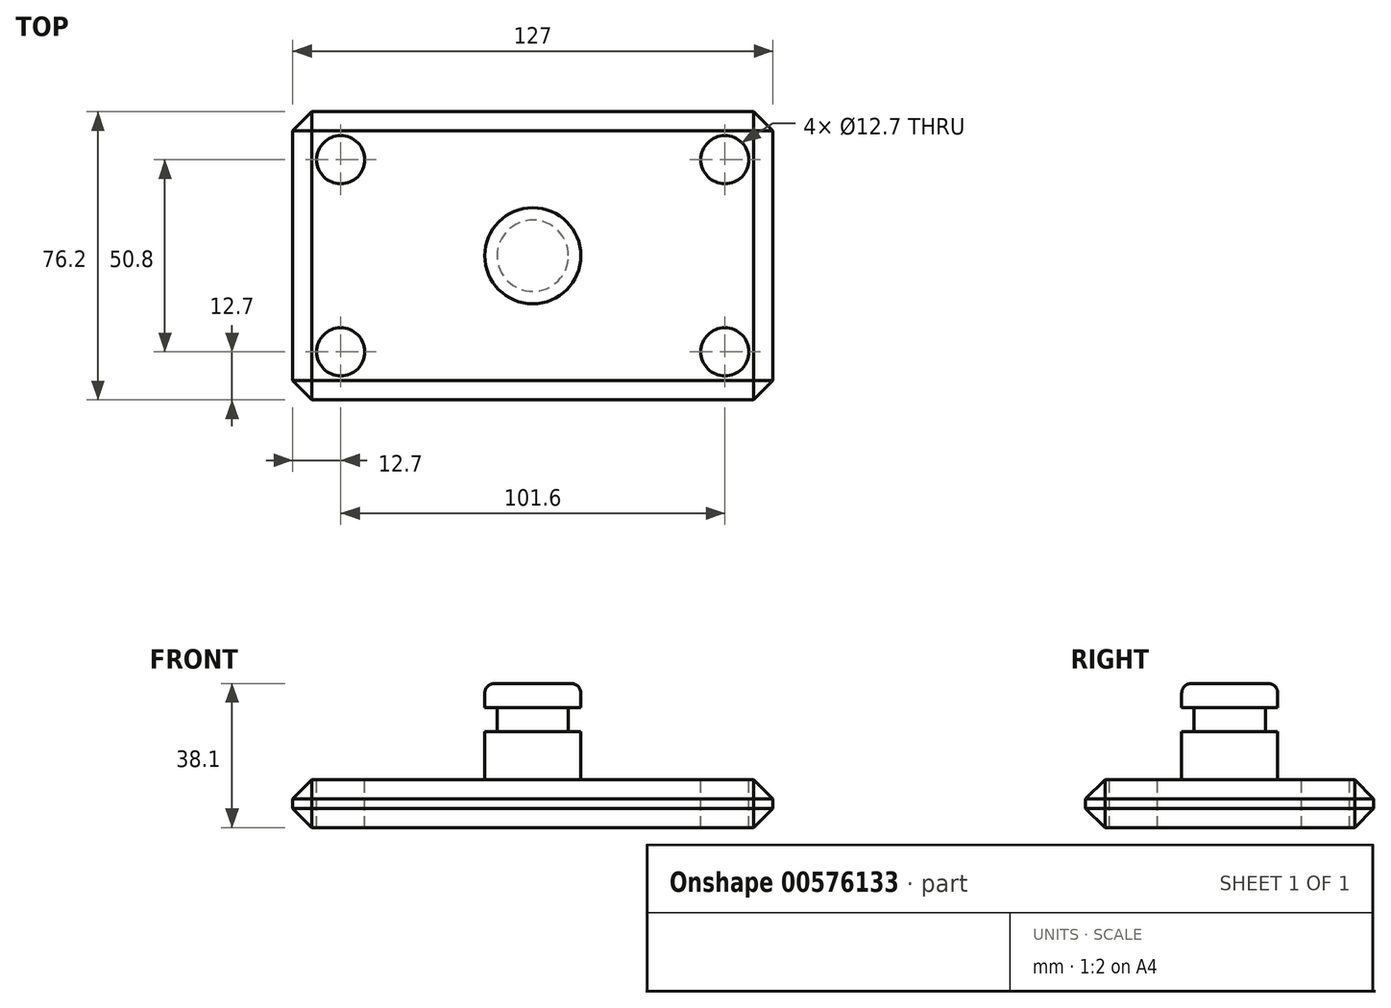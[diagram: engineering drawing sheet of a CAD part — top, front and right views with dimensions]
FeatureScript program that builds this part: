
annotation { "Feature Type Name" : "Feature", "Feature Type Description" : "" }
export const myFeature = defineFeature(function(context is Context, id is Id, definition is map)
    precondition{}
    {
        {
            var Q0;
            Q0=qCreatedBy(makeId("Top.planeOp"),FACE);
            var sketch = newSketch(context, id + "F0", { "sketchPlane" : qUnion([Q0])});
            skLineSegment(sketch, "E0.bottom", {"start": v(-63.5, 38.1) * mm, "end": v(63.5, 38.1) * mm});
            skLineSegment(sketch, "E0.top", {"start": v(-63.5, -38.1) * mm, "end": v(63.5, -38.1) * mm});
            skLineSegment(sketch, "E0.left", {"start": v(-63.5, -38.1) * mm, "end": v(-63.5, 38.1) * mm});
            skLineSegment(sketch, "E0.right", {"start": v(63.5, -38.1) * mm, "end": v(63.5, 38.1) * mm});
            skPoint(sketch, "E0.middle", {"position": v(0, 0) * mm});
            skSolve(sketch);
        }
        {
            var Q0;
            Q0=makeQuery(id+"F0.imprint","IMPRINT",FACE,{"disambiguationData":[TD([[makeQuery(id+"F0.imprint","IMPRINT",EDGE,{"derivedFrom":sQuery(id+"F0.wireOp",EDGE,"E0.bottom")}),-1.0]])]});
            extrude(context, id + "F1", {"entities" : qUnion([Q0]), "depth" : 12.7 * mm, "offsetDistance" : 25.4 * mm});
        }
        {
            var Q0;
            Q0=makeQuery(id+"F1.opExtrude","CAP_FACE",FACE,{"disambiguationData":[OSD([sQuery(id+"F0.wireOp",EDGE,"E0.bottom"),sQuery(id+"F0.wireOp",EDGE,"E0.top"),sQuery(id+"F0.wireOp",EDGE,"E0.left"),sQuery(id+"F0.wireOp",EDGE,"E0.right")])],"isStart":false});
            var sketch = newSketch(context, id + "F2", { "sketchPlane" : qUnion([Q0])});
            skCircle(sketch, "E1", {"center": v(-50.8, 25.4) * mm, "radius": 6.35 * mm});
            skCircle(sketch, "E2", {"center": v(50.8, 25.4) * mm, "radius": 6.35 * mm});
            skCircle(sketch, "E3", {"center": v(50.8, -25.4) * mm, "radius": 6.35 * mm});
            skCircle(sketch, "E4", {"center": v(-50.8, -25.4) * mm, "radius": 6.35 * mm});
            skSolve(sketch);
        }
        {
            var Q0;
            Q0=makeQuery(id+"F2.imprint","IMPRINT",FACE,{"disambiguationData":[TD([[makeQuery(id+"F2.imprint","IMPRINT",EDGE,{"derivedFrom":sQuery(id+"F2.wireOp",EDGE,"E1")}),1.0]])]});
            var Q1;
            Q1=makeQuery(id+"F2.imprint","IMPRINT",FACE,{"disambiguationData":[TD([[makeQuery(id+"F2.imprint","IMPRINT",EDGE,{"derivedFrom":sQuery(id+"F2.wireOp",EDGE,"E2")}),1.0]])]});
            var Q2;
            Q2=makeQuery(id+"F2.imprint","IMPRINT",FACE,{"disambiguationData":[TD([[makeQuery(id+"F2.imprint","IMPRINT",EDGE,{"derivedFrom":sQuery(id+"F2.wireOp",EDGE,"E3")}),1.0]])]});
            var Q3;
            Q3=makeQuery(id+"F2.imprint","IMPRINT",FACE,{"disambiguationData":[TD([[makeQuery(id+"F2.imprint","IMPRINT",EDGE,{"derivedFrom":sQuery(id+"F2.wireOp",EDGE,"E4")}),1.0]])]});
            extrude(context, id + "F3", {"entities" : qUnion([Q0, Q1, Q2, Q3]), "operationType" : NewBodyOperationType.REMOVE, "endBound" : BoundingType.THROUGH_ALL, "oppositeDirection" : true, "depth" : 25.4 * mm, "offsetDistance" : 25.4 * mm});
        }
        {
            var Q0;
            Q0=qCreatedBy(makeId("Front.planeOp"),FACE);
            var sketch = newSketch(context, id + "F4", { "sketchPlane" : qUnion([Q0])});
            skLineSegment(sketch, "E5.bottom", {"start": v(0, 12.7) * mm, "end": v(12.7, 12.7) * mm});
            skLineSegment(sketch, "E5.top", {"start": v(0, 38.1) * mm, "end": v(12.7, 38.1) * mm});
            skLineSegment(sketch, "E5.left", {"start": v(0, 12.7) * mm, "end": v(0, 38.1) * mm});
            skLineSegment(sketch, "E5.right", {"start": v(12.7, 12.7) * mm, "end": v(12.7, 38.1) * mm});
            skSolve(sketch);
        }
        {
            var Q0;
            Q0=makeQuery(id+"F4.imprint","IMPRINT",FACE,{"disambiguationData":[TD([[makeQuery(id+"F4.imprint","IMPRINT",EDGE,{"derivedFrom":sQuery(id+"F4.wireOp",EDGE,"E5.bottom")}),1.0]])]});
            var Q1;
            Q1=sQuery(id+"F4.wireOp",EDGE,"E5.left");
            revolve(context, id + "F5", {"operationType" : NewBodyOperationType.ADD, "entities" : qUnion([Q0]), "axis" : qUnion([Q1]), "revolveType" : RevolveType.FULL});
        }
        {
            var Q0;
            Q0=qCreatedBy(makeId("Front.planeOp"),FACE);
            var sketch = newSketch(context, id + "F6", { "sketchPlane" : qUnion([Q0])});
            skLineSegment(sketch, "E6.bottom", {"start": v(9.43, 31.75) * mm, "end": v(15.78, 31.75) * mm});
            skLineSegment(sketch, "E6.top", {"start": v(9.43, 25.4) * mm, "end": v(15.78, 25.4) * mm});
            skLineSegment(sketch, "E6.left", {"start": v(9.43, 31.75) * mm, "end": v(9.43, 25.4) * mm});
            skLineSegment(sketch, "E6.right", {"start": v(15.78, 31.75) * mm, "end": v(15.78, 25.4) * mm});
            skSolve(sketch);
        }
        {
            var Q0;
            Q0=makeQuery(id+"F6.imprint","IMPRINT",FACE,{"disambiguationData":[TD([[makeQuery(id+"F6.imprint","IMPRINT",EDGE,{"derivedFrom":sQuery(id+"F6.wireOp",EDGE,"E6.bottom")}),-1.0]])]});
            var Q1;
            Q1=makeQuery(id+"F5.opRevolve","SWEPT_FACE",FACE,{"disambiguationData":[OSD([sQuery(id+"F4.wireOp",EDGE,"E5.right")])]});
            revolve(context, id + "F7", {"operationType" : NewBodyOperationType.REMOVE, "entities" : qUnion([Q0]), "axis" : qUnion([Q1]), "revolveType" : RevolveType.FULL, "oppositeDirection" : true});
        }
        {
            var Q0;
            Q0=makeQuery(id+"F5.opRevolve","SWEPT_FACE",FACE,{"disambiguationData":[OSD([sQuery(id+"F4.wireOp",EDGE,"E5.top")])]});
            var Q1;
            Q1=makeQuery(id+"F5.opRevolve","SWEPT_EDGE",EDGE,{"disambiguationData":[OSD([sQuery(id+"F4.wireOp",EDGE,"E5.bottom"),sQuery(id+"F4.wireOp",EDGE,"E5.right")])]});
            var Q2;
            Q2=makeQuery(id+"F5.opRevolve","SWEPT_EDGE",EDGE,{"disambiguationData":[OSD([sQuery(id+"F4.wireOp",EDGE,"E5.top"),sQuery(id+"F4.wireOp",EDGE,"E5.right")])]});
            fillet(context, id + "F8", {"entities" : qUnion([Q0, Q1, Q2]), "radius" : 2.54 * mm, "tangentPropagation" : true, "allowEdgeOverflow" : false});
        }
        {
            var Q0;
            Q0=makeQuery(id+"F1.opExtrude","SWEPT_FACE",FACE,{"disambiguationData":[OSD([sQuery(id+"F0.wireOp",EDGE,"E0.bottom")])]});
            var Q1;
            Q1=makeQuery(id+"F1.opExtrude","SWEPT_FACE",FACE,{"disambiguationData":[OSD([sQuery(id+"F0.wireOp",EDGE,"E0.right")])]});
            var Q2;
            Q2=makeQuery(id+"F1.opExtrude","SWEPT_FACE",FACE,{"disambiguationData":[OSD([sQuery(id+"F0.wireOp",EDGE,"E0.left")])]});
            var Q3;
            Q3=makeQuery(id+"F1.opExtrude","SWEPT_FACE",FACE,{"disambiguationData":[OSD([sQuery(id+"F0.wireOp",EDGE,"E0.top")])]});
            chamfer(context, id + "F9", {"entities" : qUnion([Q0, Q1, Q2, Q3]), "width" : 5.08 * mm, "tangentPropagation" : true});
        }
    });
